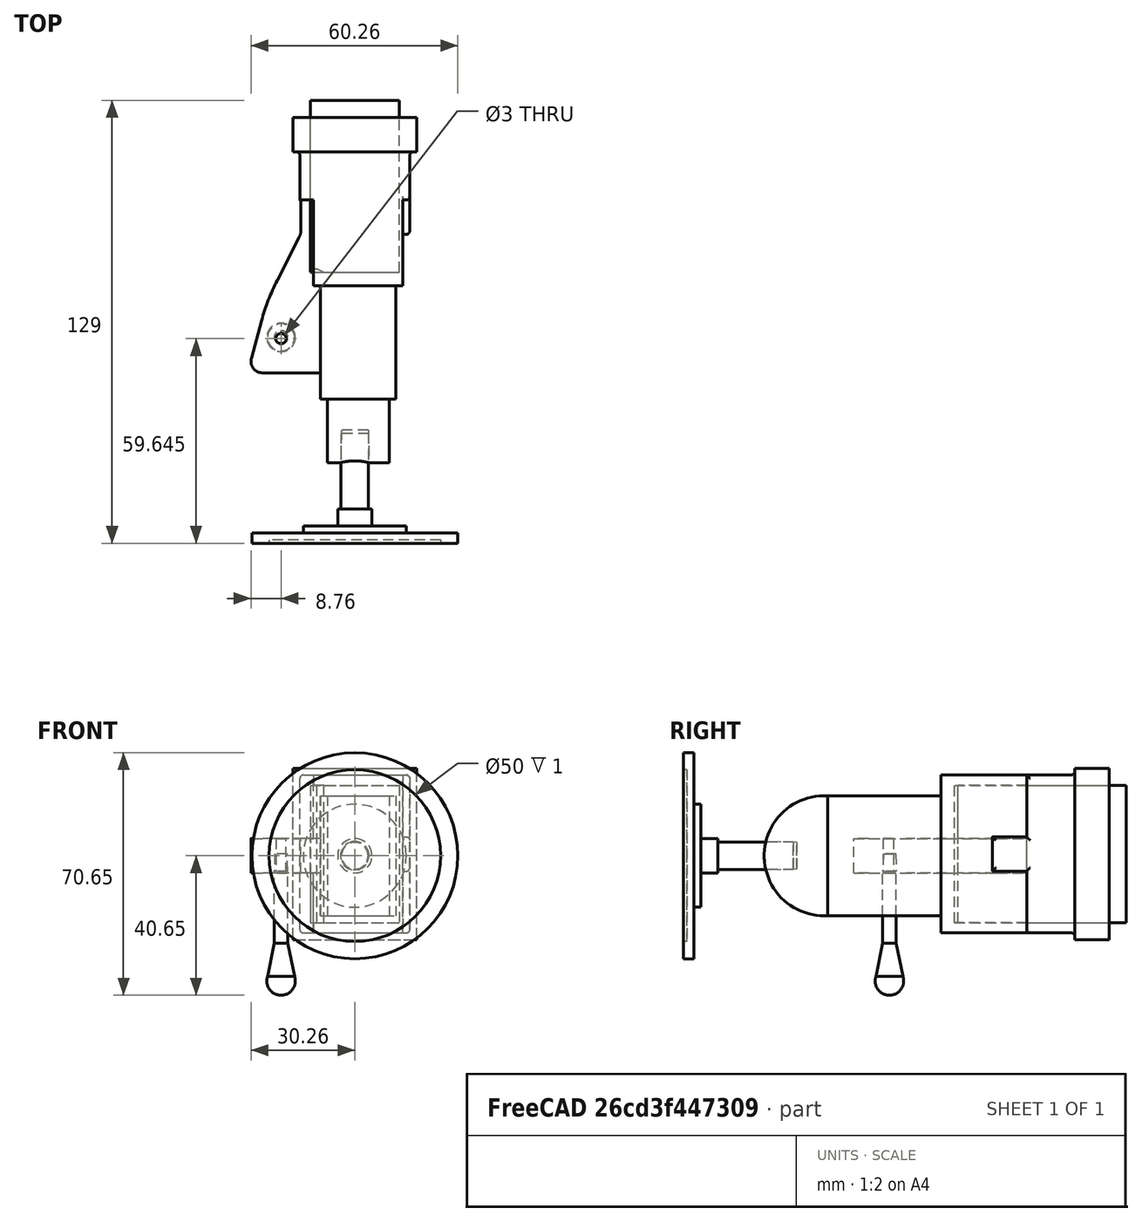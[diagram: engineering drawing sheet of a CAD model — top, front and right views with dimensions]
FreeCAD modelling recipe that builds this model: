
FCSTD DOCUMENT  (FreeCAD 0.16R6662 (Git))
Label: qtippholder-jw-rounded1
License: All rights reserved
LicenseURL: http://en.wikipedia.org/wiki/All_rights_reserved
objects: Part::Cylinder×7, Part::Box×6, Part::Cone×3, Part::MultiFuse×3, Part::Cut×3, Sketcher::SketchObject×2, App::DocumentObjectGroup×2, Mesh::Feature×1, PartDesign::Pad×1, Part::Sphere×1, PartDesign::Pocket×1, Part::Fillet×1
note: 30 computed .brp shape members not serialized (recipe doc carries the construction recipe); baked Part::Feature solids carry a one-line shape summary decoded from their .brp

FEATURE [Mesh::Feature] EarClnrHldr
  Placement = pos=(1.7939,1.69608,-3.31283) rot=(0,0,1;0rad)
FEATURE [Part::Box] Box  label="hut"
  Height = 50
  Length = 36
  Placement = pos=(14,116,11) rot=(0,0,1;0rad)
  Width = 10
FEATURE [Part::Box] Box001  label="stirn"
  Height = 46
  Length = 32
  Placement = pos=(16,102,13) rot=(0,0,1;0rad)
  Width = 17
FEATURE [Part::Box] Box002  label="gnack"
  Height = 10
  Length = 26
  Placement = pos=(22,92,31) rot=(0,0,1;0rad)
  Width = 12
FEATURE [Part::Box] Box003  label="augen"
  Height = 46
  Length = 26
  Placement = pos=(20,77,13) rot=(0,0,1;0rad)
  Width = 26
FEATURE [Part::Box] Box004  label="wangen"
  Height = 35
  Length = 22
  Placement = pos=(22,44,18) rot=(0,0,1;0rad)
  Width = 36
FEATURE [Part::Cylinder] Cylinder  label="kinn"
  Angle = 360
  Height = 18
  Placement = pos=(24,43,35.5) rot=(0,1,0;1.5708rad)
  Radius = 17.5
FEATURE [Sketcher::SketchObject] Sketch001
  Placement = pos=(22,44,36) rot=(0,0,1;0rad)
  sketch-geometry (10):
    g0: LineSegment StartX=1.5 StartY=7.67084 StartZ=0 EndX=-16.9205 EndY=7.67084 EndZ=0
    g1: LineSegment StartX=-20.1462 StartY=11.8885 StartZ=0 EndX=-17.1712 EndY=22.8519 EndZ=0
    g2: LineSegment StartX=-12.6256 StartY=34.6 StartZ=0 EndX=-6.24014 EndY=47.0658 EndZ=0
    g3: LineSegment StartX=-5.70418 StartY=49.2877 StartZ=0 EndX=-5.70418 EndY=58.874 EndZ=0
    g4: LineSegment StartX=-5.70418 StartY=58.874 StartZ=0 EndX=1.5 EndY=58.874 EndZ=0
    g5: LineSegment StartX=1.5 StartY=58.874 StartZ=0 EndX=1.5 EndY=7.67084 EndZ=0
    g6: ArcOfCircle CenterX=-16.9205 CenterY=11.0132 CenterZ=0 NormalX=0 NormalY=0 NormalZ=1 Radius=3.34236 StartAngle=2.87662 EndAngle=4.71239
    g7: ArcOfCircle CenterX=41.2664 CenterY=6.99453 CenterZ=0 NormalX=0 NormalY=0 NormalZ=1 Radius=60.5508 StartAngle=2.6682 EndAngle=2.87662
    g8: ArcOfCircle CenterX=-10.5778 CenterY=49.2877 CenterZ=0 NormalX=0 NormalY=0 NormalZ=1 Radius=4.87365 StartAngle=5.8098 EndAngle=6.28319
    g9: Circle CenterX=-11.5 CenterY=17.6445 CenterZ=0 NormalX=0 NormalY=0 NormalZ=1 Radius=1.5
  constraints (14):
    c: Horizontal(g0)
    c: Vertical(g3)
    c: Coincident(g3,g4)
    c: Horizontal(g4)
    c: Coincident(g4,g5)
    c: Coincident(g5,g0)
    c: Vertical(g5)
    c: Tangent(g0,g6) = 1.5708
    c: Tangent(g1,g6) = 1.5708
    c: Tangent(g1,g7) = 1.5708
    c: Tangent(g2,g7) = 1.5708
    c: Tangent(g2,g8) = -1.5708
    c: Tangent(g3,g8) = -1.5708
    c: Radius(g9) = 1.5
FEATURE [PartDesign::Pad] Pad  label="nase"
  Length = 4.5
  Length2 = 5.5
  Placement = pos=(22,44,36) rot=(0,0,1;0rad)
  Sketch = -> Sketch001
  Type = 4
FEATURE [Part::Cylinder] Cylinder002  label="bein006"
  Angle = 360
  Height = 32
  Placement = pos=(32,34,35.5) rot=(1,0,0;1.5708rad)
  Radius = 4
FEATURE [Part::Cylinder] Cylinder003  label="bein001"
  Angle = 360
  Height = 11
  Placement = pos=(32,12,35.5) rot=(1,0,0;1.5708rad)
  Radius = 5
FEATURE [Part::Cylinder] Cylinder004  label="bein002"
  Angle = 360
  Height = 4
  Placement = pos=(32,7,35.5) rot=(1,0,0;1.5708rad)
  Radius = 15
FEATURE [Part::Cylinder] Cylinder005  label="bein003"
  Angle = 360
  Height = 3
  Placement = pos=(32,5,35.5) rot=(1,0,0;1.5708rad)
  Radius = 30
FEATURE [Part::Cylinder] Cylinder006  label="bein004"
  Angle = 360
  Height = 3
  Placement = pos=(32,3,35.5) rot=(1,0,0;1.5708rad)
  Radius = 25
FEATURE [Part::Box] Box005  label="kopfloch"
  Height = 40
  Length = 26
  Placement = pos=(19,81,16) rot=(0,0,1;0rad)
  Width = 50
FEATURE [Part::Cylinder] Cylinder007  label="staebchen"
  Angle = 360
  Height = 27
  Placement = pos=(10.5,62,4) rot=(0,0,1;0rad)
  Radius = 2
FEATURE [Part::Sphere] Sphere  label="Kugel"
  Angle1 = -90
  Angle2 = 90
  Angle3 = 360
  Placement = pos=(10.5,62,-1) rot=(0,0,1;0rad)
  Radius = 4.15
FEATURE [Part::Cone] Cone  label="Kegel"
  Angle = 360
  Height = 10
  Placement = pos=(10.5,62,0) rot=(0,0,1;0rad)
  Radius1 = 4
  Radius2 = 2
FEATURE [Part::Cone] Cone001  label="Kegel001"
  Angle = 360
  Height = 5
  Placement = pos=(10.5,62,31) rot=(0,0,1;0rad)
  Radius1 = 2
  Radius2 = 1.8
FEATURE [Part::Cone] Cone002  label="beinloch001"
  Angle = 360
  Height = 11
  Placement = pos=(32,35,35.5) rot=(1,0,0;1.5708rad)
  Radius1 = 3.9
  Radius2 = 4.2
FEATURE [Part::MultiFuse] Fusion
  Shapes = -> [Box,Box001,Box002,Box003,Box004,Cylinder,Pad]
FEATURE [Part::MultiFuse] Fusion001
  Shapes = -> [Cone001,Cylinder007,Sphere,Cone]
FEATURE [App::DocumentObjectGroup] Gruppe001  label="halb-qtipp"
  Group = -> [Fusion001]
FEATURE [Part::MultiFuse] Fusion002
  Shapes = -> [Cylinder002,Cylinder003,Cylinder005,Cylinder004]
FEATURE [Part::Cut] Cut002
  Base = -> Fusion002
  Tool = -> Cylinder006
FEATURE [App::DocumentObjectGroup] Gruppe  label="bein"
  Group = -> [Cut002]
FEATURE [Sketcher::SketchObject] Sketch
  Placement = pos=(19,81,16) rot=(1,0,0;3.14159rad)
  Support = -> Box005 [Face5]
  sketch-geometry (4):
    g0: LineSegment StartX=0 StartY=0 StartZ=0 EndX=0 EndY=-1 EndZ=0
    g1: LineSegment StartX=0 StartY=-1 StartZ=0 EndX=2 EndY=-1 EndZ=0
    g2: LineSegment StartX=2 StartY=-1 StartZ=0 EndX=4 EndY=0 EndZ=0
    g3: LineSegment StartX=4 StartY=0 StartZ=0 EndX=0 EndY=0 EndZ=0
  constraints (11):
    c: Coincident(g-1,g0)
    c: PointOnObject(g0,g-2)
    c: Coincident(g0,g1)
    c: Horizontal(g1)
    c: Coincident(g1,g2)
    c: Coincident(g2,g3)
    c: Coincident(g3,g0)
    c: Horizontal(g3)
    c: DistanceY(g0,g0) = 1
    c: DistanceX(g1,g1) = 2
    c: DistanceX(g3,g3) = 4
FEATURE [PartDesign::Pocket] Pocket
  Length = 5
  Placement = pos=(19,81,16) rot=(0,0,1;0rad)
  Sketch = -> Sketch
  Type = 1
FEATURE [Part::Cut] Cut
  Base = -> Fusion
  Tool = -> Pocket
FEATURE [Part::Cut] Cut003  label="kopf"
  Base = -> Cut
  Tool = -> Cone002
FEATURE [Part::Fillet] Fillet
  Base = -> Cut003
  Edges = 14 edges r=4: [Edge90,Edge91,Edge92,Edge93,Edge94,Edge95,Edge96,Edge111,Edge119,Edge120,Edge123,Edge125,Edge126,Edge127]
